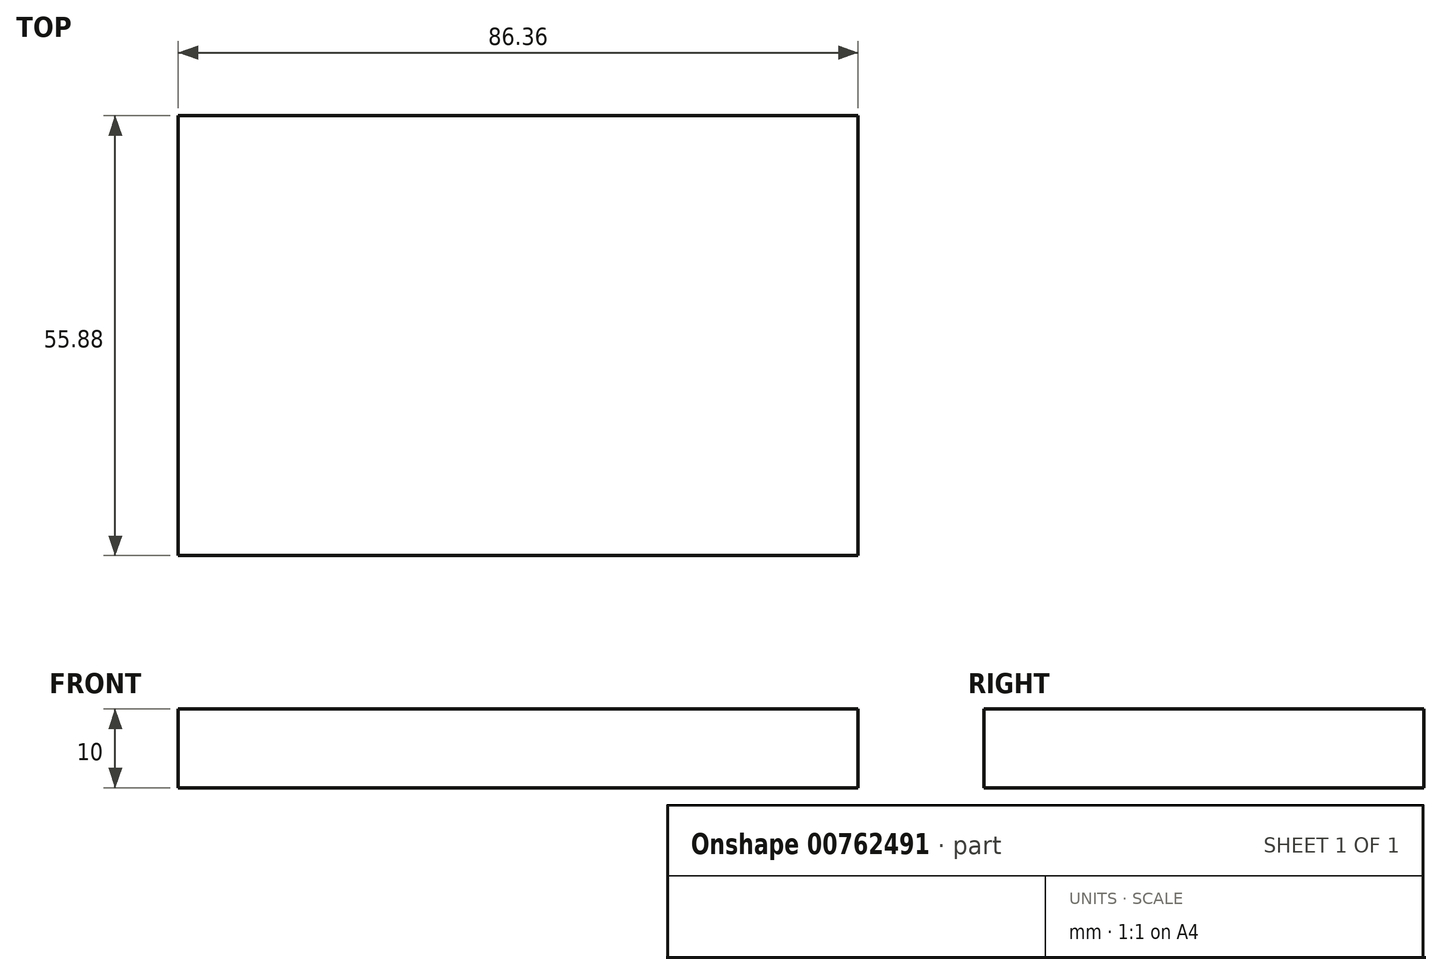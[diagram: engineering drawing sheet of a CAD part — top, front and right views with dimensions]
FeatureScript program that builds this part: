
annotation { "Feature Type Name" : "Feature", "Feature Type Description" : "" }
export const myFeature = defineFeature(function(context is Context, id is Id, definition is map)
    precondition{}
    {
        {
            var Q0;
            Q0=qCreatedBy(makeId("Top.planeOp"),FACE);
            var sketch = newSketch(context, id + "F0", { "sketchPlane" : qUnion([Q0])});
            skLineSegment(sketch, "E0.bottom", {"start": v(0, 0) * mm, "end": v(86.36, 0) * mm});
            skLineSegment(sketch, "E0.top", {"start": v(0, 55.88) * mm, "end": v(86.36, 55.88) * mm});
            skLineSegment(sketch, "E0.left", {"start": v(0, 0) * mm, "end": v(0, 55.88) * mm});
            skLineSegment(sketch, "E0.right", {"start": v(86.36, 0) * mm, "end": v(86.36, 55.88) * mm});
            skSolve(sketch);
        }
        {
            var Q0;
            Q0=makeQuery(id+"F0.imprint","IMPRINT",FACE,{"disambiguationData":[TD([[makeQuery(id+"F0.imprint","IMPRINT",EDGE,{"derivedFrom":sQuery(id+"F0.wireOp",EDGE,"E0.bottom")}),1.0]])]});
            extrude(context, id + "F1", {"entities" : qUnion([Q0]), "depth" : 10 * mm, "offsetDistance" : 25.4 * mm});
        }
    });
